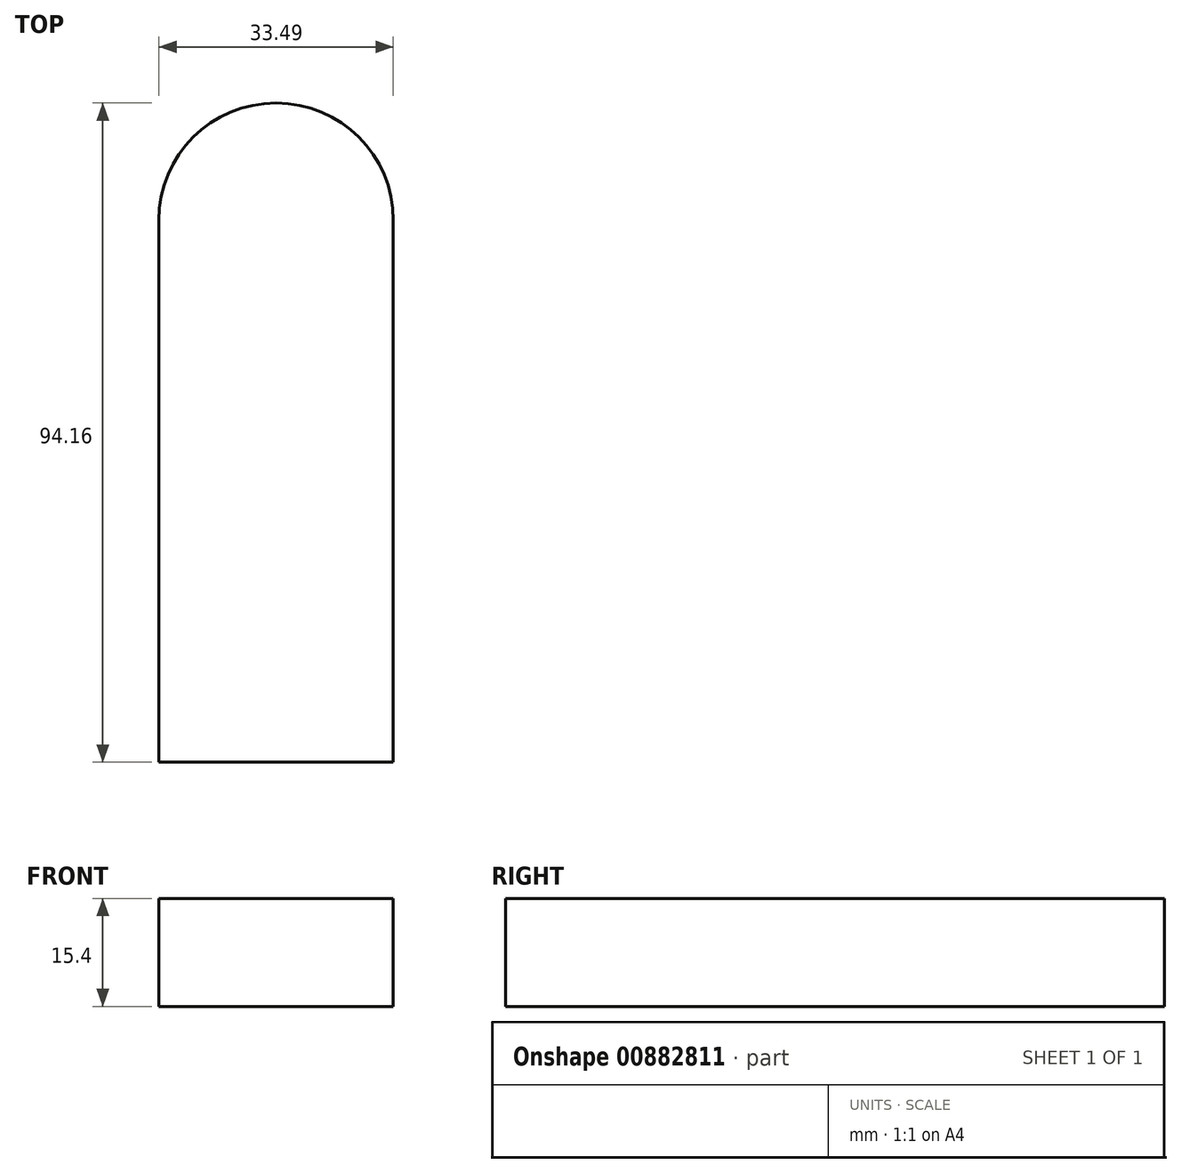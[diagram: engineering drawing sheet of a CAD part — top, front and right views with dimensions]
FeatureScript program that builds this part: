
annotation { "Feature Type Name" : "Feature", "Feature Type Description" : "" }
export const myFeature = defineFeature(function(context is Context, id is Id, definition is map)
    precondition{}
    {
        {
            var Q0;
            Q0=qCreatedBy(makeId("Top.planeOp"),FACE);
            var sketch = newSketch(context, id + "F0", { "sketchPlane" : qUnion([Q0])});
            skLineSegment(sketch, "E0.bottom", {"start": v(-16.62, -40.77) * mm, "end": v(16.87, -40.77) * mm});
            skLineSegment(sketch, "E0.top", {"start": v(-16.62, 36.64) * mm, "end": v(16.87, 36.64) * mm});
            skLineSegment(sketch, "E0.left", {"start": v(-16.62, -40.77) * mm, "end": v(-16.62, 36.64) * mm});
            skLineSegment(sketch, "E0.right", {"start": v(16.87, -40.77) * mm, "end": v(16.87, 36.64) * mm});
            skArc(sketch, "E1", {"start": v(16.87, 36.64) * mm, "mid": v(0.12, 53.39) * mm, "end": v(-16.62, 36.64) * mm});
            skSolve(sketch);
        }
        {
            var Q0;
            Q0 = qSketchRegion(id + "F0", true);
            var Q1;
            Q1=makeQuery(id+"F0.imprint","IMPRINT",FACE,{"disambiguationData":[TD([[makeQuery(id+"F0.imprint","IMPRINT",EDGE,{"derivedFrom":sQuery(id+"F0.wireOp",EDGE,"E0.top")}),1.0]])]});
            extrude(context, id + "F1", {"entities" : qUnion([Q0, Q1]), "depth" : 15.4 * mm, "offsetDistance" : 25 * mm});
        }
    });
